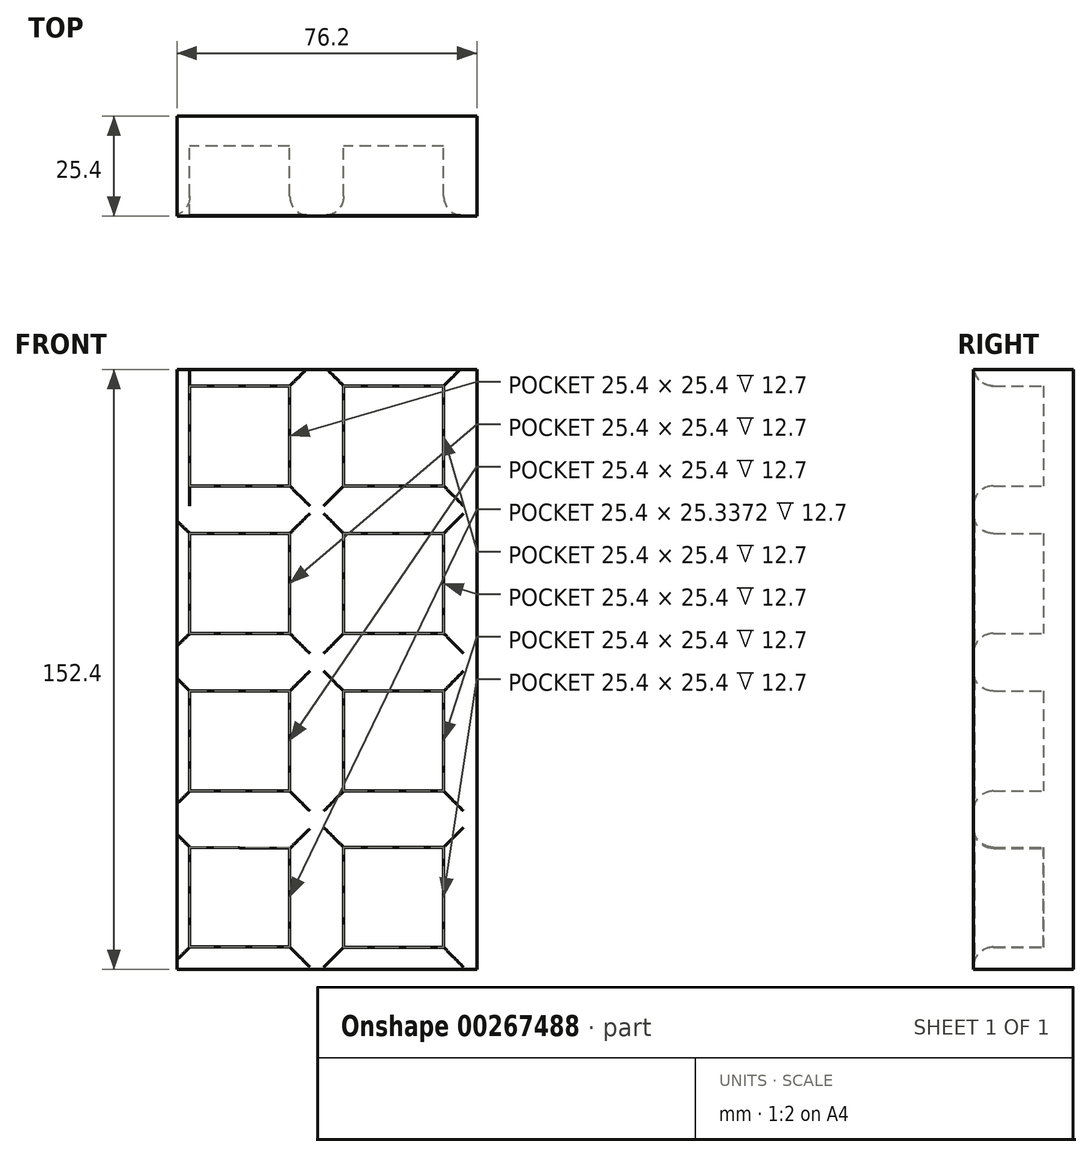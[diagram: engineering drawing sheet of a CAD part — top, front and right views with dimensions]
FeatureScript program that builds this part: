
annotation { "Feature Type Name" : "Feature", "Feature Type Description" : "" }
export const myFeature = defineFeature(function(context is Context, id is Id, definition is map)
    precondition{}
    {
        {
            var Q0;
            Q0=qCreatedBy(makeId("Front.planeOp"),FACE);
            var sketch = newSketch(context, id + "F0", { "sketchPlane" : qUnion([Q0])});
            skLineSegment(sketch, "E0.bottom", {"start": v(38.1, 76.2) * mm, "end": v(-38.1, 76.2) * mm});
            skLineSegment(sketch, "E0.top", {"start": v(38.1, -76.2) * mm, "end": v(-38.1, -76.2) * mm});
            skLineSegment(sketch, "E0.left", {"start": v(38.1, 76.2) * mm, "end": v(38.1, -76.2) * mm});
            skLineSegment(sketch, "E0.right", {"start": v(-38.1, 76.2) * mm, "end": v(-38.1, -76.2) * mm});
            skPoint(sketch, "E0.middle", {"position": v(0, 0) * mm});
            skLineSegment(sketch, "E1", {"start": v(-34.8, 72.04) * mm, "end": v(-34.8, 46.64) * mm});
            skLineSegment(sketch, "E2", {"start": v(-34.8, 46.64) * mm, "end": v(-9.4, 46.64) * mm});
            skLineSegment(sketch, "E3", {"start": v(-9.4, 46.64) * mm, "end": v(-9.4, 72.04) * mm});
            skLineSegment(sketch, "E4", {"start": v(-9.4, 72.04) * mm, "end": v(-34.8, 72.04) * mm});
            skLineSegment(sketch, "E5", {"start": v(-34.8, 34.56) * mm, "end": v(-34.8, 9.16) * mm});
            skPoint(sketch, "E5.startSnap0", {"position": v(-34.8, 59.34) * mm});
            skLineSegment(sketch, "E6", {"start": v(-34.8, 9.16) * mm, "end": v(-9.4, 9.16) * mm});
            skLineSegment(sketch, "E7", {"start": v(-9.4, 9.16) * mm, "end": v(-9.4, 34.56) * mm});
            skLineSegment(sketch, "E8", {"start": v(-9.4, 34.56) * mm, "end": v(-34.8, 34.56) * mm});
            skLineSegment(sketch, "E9", {"start": v(-34.8, -5.5) * mm, "end": v(-34.8, -30.9) * mm});
            skLineSegment(sketch, "E10", {"start": v(-34.8, -30.9) * mm, "end": v(-9.4, -30.9) * mm});
            skLineSegment(sketch, "E11", {"start": v(-9.4, -30.9) * mm, "end": v(-9.4, -5.5) * mm});
            skLineSegment(sketch, "E12", {"start": v(-9.4, -5.5) * mm, "end": v(-34.8, -5.5) * mm});
            skLineSegment(sketch, "E13", {"start": v(-34.8, -45.18) * mm, "end": v(-34.8, -70.52) * mm});
            skLineSegment(sketch, "E14", {"start": v(-34.8, -70.52) * mm, "end": v(-9.4, -70.52) * mm});
            skLineSegment(sketch, "E15", {"start": v(-9.4, -70.52) * mm, "end": v(-9.4, -45.48) * mm});
            skLineSegment(sketch, "E16", {"start": v(-9.4, -45.48) * mm, "end": v(-34.8, -45.18) * mm});
            skLineSegment(sketch, "E17", {"start": v(4.27, 72.04) * mm, "end": v(4.27, 46.64) * mm});
            skLineSegment(sketch, "E18", {"start": v(4.27, 46.64) * mm, "end": v(29.67, 46.64) * mm});
            skLineSegment(sketch, "E19", {"start": v(29.67, 46.64) * mm, "end": v(29.67, 72.04) * mm});
            skLineSegment(sketch, "E20", {"start": v(29.67, 72.04) * mm, "end": v(4.27, 72.04) * mm});
            skLineSegment(sketch, "E21", {"start": v(4.27, 34.56) * mm, "end": v(4.27, 9.16) * mm});
            skLineSegment(sketch, "E22", {"start": v(4.27, 9.16) * mm, "end": v(29.67, 9.16) * mm});
            skLineSegment(sketch, "E23", {"start": v(29.67, 9.16) * mm, "end": v(29.67, 34.56) * mm});
            skLineSegment(sketch, "E24", {"start": v(29.67, 34.56) * mm, "end": v(4.27, 34.56) * mm});
            skLineSegment(sketch, "E25", {"start": v(4.27, -5.5) * mm, "end": v(4.27, -30.9) * mm});
            skLineSegment(sketch, "E26", {"start": v(4.27, -30.9) * mm, "end": v(29.67, -30.9) * mm});
            skLineSegment(sketch, "E27", {"start": v(29.67, -30.9) * mm, "end": v(29.67, -5.5) * mm});
            skLineSegment(sketch, "E28", {"start": v(29.67, -5.5) * mm, "end": v(4.27, -5.5) * mm});
            skLineSegment(sketch, "E29", {"start": v(4.27, -45.18) * mm, "end": v(4.27, -70.58) * mm});
            skLineSegment(sketch, "E30", {"start": v(4.27, -70.58) * mm, "end": v(29.67, -70.58) * mm});
            skLineSegment(sketch, "E31", {"start": v(29.67, -70.58) * mm, "end": v(29.67, -45.18) * mm});
            skLineSegment(sketch, "E32", {"start": v(29.67, -45.18) * mm, "end": v(4.27, -45.18) * mm});
            skSolve(sketch);
        }
        {
            var Q0;
            Q0=makeQuery(id+"F0.imprint","IMPRINT",FACE,{"disambiguationData":[TD([[makeQuery(id+"F0.imprint","IMPRINT",EDGE,{"derivedFrom":sQuery(id+"F0.wireOp",EDGE,"E0.bottom")}),1.0]])]});
            extrude(context, id + "F1", {"entities" : qUnion([Q0]), "depth" : 25.4 * mm});
        }
        {
            var Q0;
            Q0=makeQuery(id+"F0.imprint","IMPRINT",FACE,{"disambiguationData":[TD([[makeQuery(id+"F0.imprint","IMPRINT",EDGE,{"derivedFrom":sQuery(id+"F0.wireOp",EDGE,"E1")}),1.0]])]});
            var Q1;
            Q1=makeQuery(id+"F0.imprint","IMPRINT",FACE,{"disambiguationData":[TD([[makeQuery(id+"F0.imprint","IMPRINT",EDGE,{"derivedFrom":sQuery(id+"F0.wireOp",EDGE,"E17")}),1.0]])]});
            var Q2;
            Q2=makeQuery(id+"F0.imprint","IMPRINT",FACE,{"disambiguationData":[TD([[makeQuery(id+"F0.imprint","IMPRINT",EDGE,{"derivedFrom":sQuery(id+"F0.wireOp",EDGE,"E21")}),1.0]])]});
            var Q3;
            Q3=makeQuery(id+"F0.imprint","IMPRINT",FACE,{"disambiguationData":[TD([[makeQuery(id+"F0.imprint","IMPRINT",EDGE,{"derivedFrom":sQuery(id+"F0.wireOp",EDGE,"E5")}),1.0]])]});
            var Q4;
            Q4=makeQuery(id+"F0.imprint","IMPRINT",FACE,{"disambiguationData":[TD([[makeQuery(id+"F0.imprint","IMPRINT",EDGE,{"derivedFrom":sQuery(id+"F0.wireOp",EDGE,"E9")}),1.0]])]});
            var Q5;
            Q5=makeQuery(id+"F0.imprint","IMPRINT",FACE,{"disambiguationData":[TD([[makeQuery(id+"F0.imprint","IMPRINT",EDGE,{"derivedFrom":sQuery(id+"F0.wireOp",EDGE,"E25")}),1.0]])]});
            var Q6;
            Q6=makeQuery(id+"F0.imprint","IMPRINT",FACE,{"disambiguationData":[TD([[makeQuery(id+"F0.imprint","IMPRINT",EDGE,{"derivedFrom":sQuery(id+"F0.wireOp",EDGE,"E29")}),1.0]])]});
            var Q7;
            Q7=makeQuery(id+"F0.imprint","IMPRINT",FACE,{"disambiguationData":[TD([[makeQuery(id+"F0.imprint","IMPRINT",EDGE,{"derivedFrom":sQuery(id+"F0.wireOp",EDGE,"E13")}),1.0]])]});
            extrude(context, id + "F2", {"entities" : qUnion([Q0, Q1, Q2, Q3, Q4, Q5, Q6, Q7]), "operationType" : NewBodyOperationType.ADD, "depth" : 7.62 * mm});
        }
        {
            var Q0;
            Q0=makeQuery(id+"F1.opExtrude","CAP_EDGE",EDGE,{"disambiguationData":[OSD([sQuery(id+"F0.wireOp",EDGE,"E19")])],"isStart":false});
            var Q1;
            Q1=makeQuery(id+"F1.opExtrude","CAP_EDGE",EDGE,{"disambiguationData":[OSD([sQuery(id+"F0.wireOp",EDGE,"E20")])],"isStart":false});
            var Q2;
            Q2=makeQuery(id+"F1.opExtrude","CAP_EDGE",EDGE,{"disambiguationData":[OSD([sQuery(id+"F0.wireOp",EDGE,"E17")])],"isStart":false});
            var Q3;
            Q3=makeQuery(id+"F1.opExtrude","CAP_EDGE",EDGE,{"disambiguationData":[OSD([sQuery(id+"F0.wireOp",EDGE,"E18")])],"isStart":false});
            var Q4;
            Q4=makeQuery(id+"F1.opExtrude","CAP_EDGE",EDGE,{"disambiguationData":[OSD([sQuery(id+"F0.wireOp",EDGE,"E4")])],"isStart":false});
            var Q5;
            Q5=makeQuery(id+"F1.opExtrude","CAP_EDGE",EDGE,{"disambiguationData":[OSD([sQuery(id+"F0.wireOp",EDGE,"E2")])],"isStart":false});
            var Q6;
            Q6=makeQuery(id+"F1.opExtrude","CAP_EDGE",EDGE,{"disambiguationData":[OSD([sQuery(id+"F0.wireOp",EDGE,"E3")])],"isStart":false});
            var Q7;
            Q7=makeQuery(id+"F2.opExtrude","CAP_EDGE",EDGE,{"disambiguationData":[OSD([sQuery(id+"F0.wireOp",EDGE,"E1")])],"isStart":false});
            var Q8;
            Q8=makeQuery(id+"F1.opExtrude","CAP_EDGE",EDGE,{"disambiguationData":[OSD([sQuery(id+"F0.wireOp",EDGE,"E7")])],"isStart":false});
            var Q9;
            Q9=makeQuery(id+"F1.opExtrude","CAP_EDGE",EDGE,{"disambiguationData":[OSD([sQuery(id+"F0.wireOp",EDGE,"E8")])],"isStart":false});
            var Q10;
            Q10=makeQuery(id+"F1.opExtrude","CAP_EDGE",EDGE,{"disambiguationData":[OSD([sQuery(id+"F0.wireOp",EDGE,"E5")])],"isStart":false});
            var Q11;
            Q11=makeQuery(id+"F1.opExtrude","CAP_EDGE",EDGE,{"disambiguationData":[OSD([sQuery(id+"F0.wireOp",EDGE,"E6")])],"isStart":false});
            var Q12;
            Q12=makeQuery(id+"F1.opExtrude","CAP_EDGE",EDGE,{"disambiguationData":[OSD([sQuery(id+"F0.wireOp",EDGE,"E12")])],"isStart":false});
            var Q13;
            Q13=makeQuery(id+"F1.opExtrude","CAP_EDGE",EDGE,{"disambiguationData":[OSD([sQuery(id+"F0.wireOp",EDGE,"E11")])],"isStart":false});
            var Q14;
            Q14=makeQuery(id+"F1.opExtrude","CAP_EDGE",EDGE,{"disambiguationData":[OSD([sQuery(id+"F0.wireOp",EDGE,"E10")])],"isStart":false});
            var Q15;
            Q15=makeQuery(id+"F1.opExtrude","CAP_EDGE",EDGE,{"disambiguationData":[OSD([sQuery(id+"F0.wireOp",EDGE,"E9")])],"isStart":false});
            var Q16;
            Q16=makeQuery(id+"F1.opExtrude","CAP_EDGE",EDGE,{"disambiguationData":[OSD([sQuery(id+"F0.wireOp",EDGE,"E28")])],"isStart":false});
            var Q17;
            Q17=makeQuery(id+"F1.opExtrude","CAP_EDGE",EDGE,{"disambiguationData":[OSD([sQuery(id+"F0.wireOp",EDGE,"E26")])],"isStart":false});
            var Q18;
            Q18=makeQuery(id+"F1.opExtrude","CAP_EDGE",EDGE,{"disambiguationData":[OSD([sQuery(id+"F0.wireOp",EDGE,"E27")])],"isStart":false});
            var Q19;
            Q19=makeQuery(id+"F1.opExtrude","CAP_EDGE",EDGE,{"disambiguationData":[OSD([sQuery(id+"F0.wireOp",EDGE,"E25")])],"isStart":false});
            var Q20;
            Q20=makeQuery(id+"F1.opExtrude","CAP_EDGE",EDGE,{"disambiguationData":[OSD([sQuery(id+"F0.wireOp",EDGE,"E21")])],"isStart":false});
            var Q21;
            Q21=makeQuery(id+"F1.opExtrude","CAP_EDGE",EDGE,{"disambiguationData":[OSD([sQuery(id+"F0.wireOp",EDGE,"E24")])],"isStart":false});
            var Q22;
            Q22=makeQuery(id+"F1.opExtrude","CAP_EDGE",EDGE,{"disambiguationData":[OSD([sQuery(id+"F0.wireOp",EDGE,"E32")])],"isStart":false});
            var Q23;
            Q23=makeQuery(id+"F1.opExtrude","CAP_EDGE",EDGE,{"disambiguationData":[OSD([sQuery(id+"F0.wireOp",EDGE,"E31")])],"isStart":false});
            var Q24;
            Q24=makeQuery(id+"F1.opExtrude","CAP_EDGE",EDGE,{"disambiguationData":[OSD([sQuery(id+"F0.wireOp",EDGE,"E30")])],"isStart":false});
            var Q25;
            Q25=makeQuery(id+"F1.opExtrude","CAP_EDGE",EDGE,{"disambiguationData":[OSD([sQuery(id+"F0.wireOp",EDGE,"E29")])],"isStart":false});
            var Q26;
            Q26=makeQuery(id+"F1.opExtrude","CAP_EDGE",EDGE,{"disambiguationData":[OSD([sQuery(id+"F0.wireOp",EDGE,"E16")])],"isStart":false});
            var Q27;
            Q27=makeQuery(id+"F1.opExtrude","CAP_EDGE",EDGE,{"disambiguationData":[OSD([sQuery(id+"F0.wireOp",EDGE,"E15")])],"isStart":false});
            var Q28;
            Q28=makeQuery(id+"F1.opExtrude","CAP_EDGE",EDGE,{"disambiguationData":[OSD([sQuery(id+"F0.wireOp",EDGE,"E14")])],"isStart":false});
            var Q29;
            Q29=makeQuery(id+"F1.opExtrude","CAP_EDGE",EDGE,{"disambiguationData":[OSD([sQuery(id+"F0.wireOp",EDGE,"E13")])],"isStart":false});
            var Q30;
            Q30=makeQuery(id+"F1.opExtrude","CAP_EDGE",EDGE,{"disambiguationData":[OSD([sQuery(id+"F0.wireOp",EDGE,"E23")])],"isStart":false});
            var Q31;
            Q31=makeQuery(id+"F1.opExtrude","CAP_EDGE",EDGE,{"disambiguationData":[OSD([sQuery(id+"F0.wireOp",EDGE,"E22")])],"isStart":false});
            fillet(context, id + "F3", {"entities" : qUnion([Q0, Q1, Q2, Q3, Q4, Q5, Q6, Q7, Q8, Q9, Q10, Q11, Q12, Q13, Q14, Q15, Q16, Q17, Q18, Q19, Q20, Q21, Q22, Q23, Q24, Q25, Q26, Q27, Q28, Q29, Q30, Q31]), "radius" : 5.08 * mm, "tangentPropagation" : true, "allowEdgeOverflow" : false});
        }
    });
